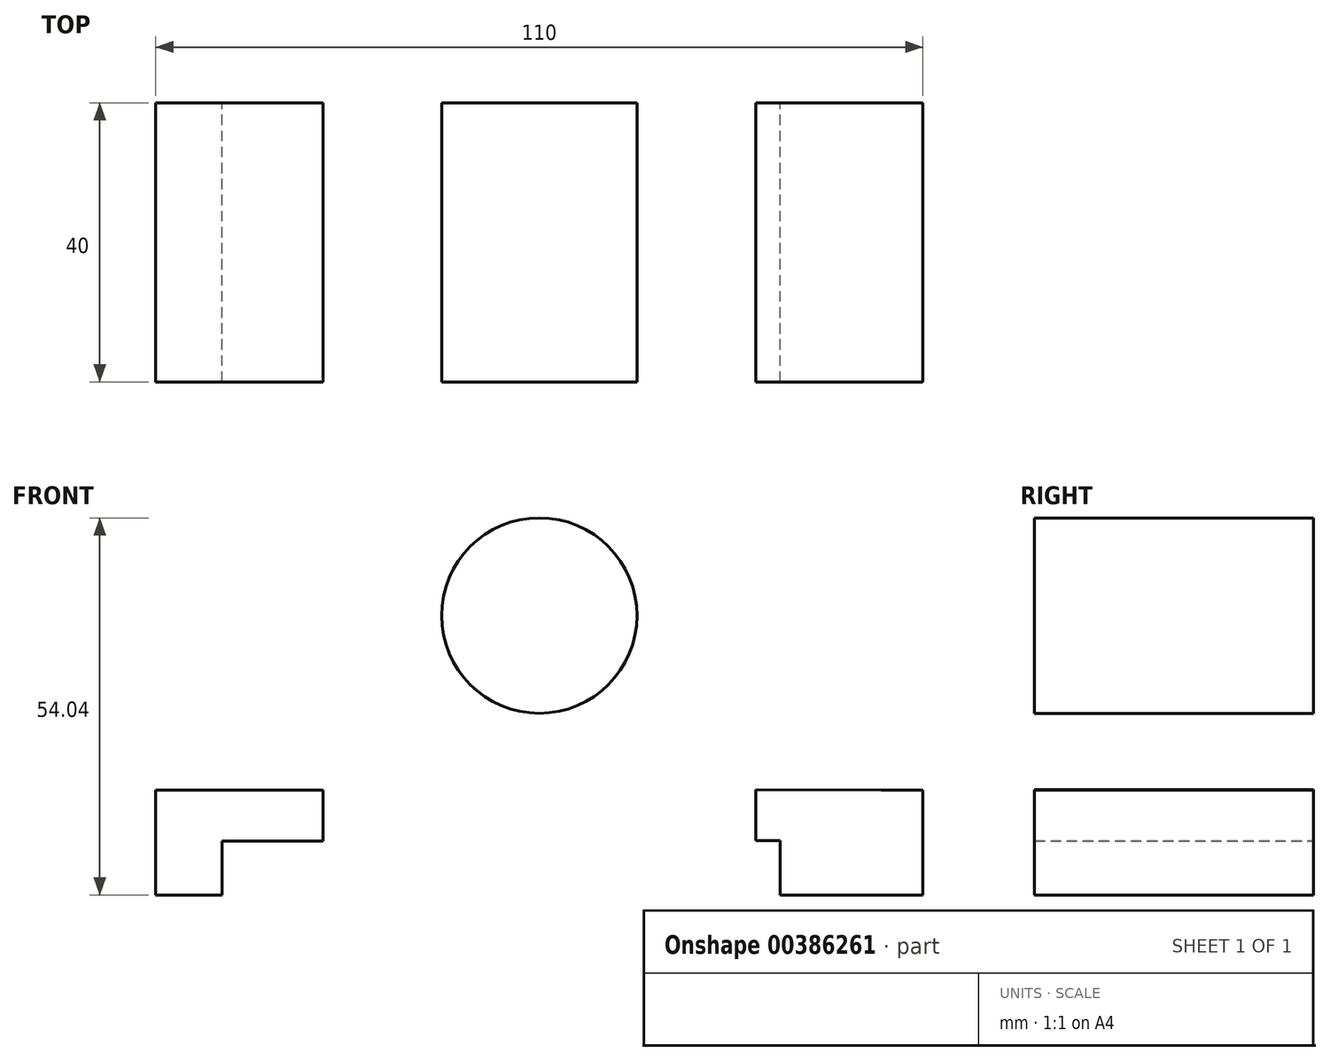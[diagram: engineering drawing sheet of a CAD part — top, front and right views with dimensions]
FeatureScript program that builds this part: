
annotation { "Feature Type Name" : "Feature", "Feature Type Description" : "" }
export const myFeature = defineFeature(function(context is Context, id is Id, definition is map)
    precondition{}
    {
        {
            var Q0;
            Q0=qCreatedBy(makeId("Front.planeOp"),FACE);
            var sketch = newSketch(context, id + "F0", { "sketchPlane" : qUnion([Q0])});
            skLineSegment(sketch, "E0", {"start": v(-42.27, 0) * mm, "end": v(67.73, 0) * mm});
            skLineSegment(sketch, "E1", {"start": v(67.73, 0) * mm, "end": v(67.73, 15) * mm});
            skLineSegment(sketch, "E2", {"start": v(37.73, 15.08) * mm, "end": v(37.73, 40.08) * mm});
            skLineSegment(sketch, "E3", {"start": v(-42.27, 0) * mm, "end": v(-42.27, 15) * mm});
            skLineSegment(sketch, "E4", {"start": v(-12.27, 15) * mm, "end": v(-12.27, 40) * mm});
            skLineSegment(sketch, "E5", {"start": v(-12.27, 40) * mm, "end": v(37.73, 40.08) * mm, "construction": true});
            skPoint(sketch, "E6", {"position": v(12.73, 40.04) * mm});
            skCircle(sketch, "E7", {"center": v(12.73, 40.04) * mm, "radius": 14 * mm});
            skPoint(sketch, "E8.endSnap0", {"position": v(-42.27, 7.5) * mm});
            skArc(sketch, "E9", {"start": v(37.73, 40) * mm, "mid": v(12.73, 65.04) * mm, "end": v(-12.27, 40) * mm});
            skLineSegment(sketch, "E10", {"start": v(-42.27, 15) * mm, "end": v(-12.27, 15) * mm});
            skLineSegment(sketch, "E11", {"start": v(-12.27, 15) * mm, "end": v(-18.27, 15) * mm});
            skLineSegment(sketch, "E12", {"start": v(-42.27, 15) * mm, "end": v(-36.27, 15) * mm});
            skLineSegment(sketch, "E13", {"start": v(-42.27, 0) * mm, "end": v(-32.77, 0) * mm});
            skLineSegment(sketch, "E14", {"start": v(-32.77, 0) * mm, "end": v(-21.77, 0) * mm});
            skLineSegment(sketch, "E15", {"start": v(-36.27, 15) * mm, "end": v(-36.27, 7.7) * mm});
            skLineSegment(sketch, "E16", {"start": v(-18.27, 15) * mm, "end": v(-18.27, 7.7) * mm});
            skLineSegment(sketch, "E17", {"start": v(-36.27, 7.7) * mm, "end": v(-18.27, 7.7) * mm});
            skLineSegment(sketch, "E18", {"start": v(-32.77, 0) * mm, "end": v(-32.77, 7.7) * mm});
            skLineSegment(sketch, "E19", {"start": v(-21.77, 0) * mm, "end": v(-21.77, 7.7) * mm});
            skLineSegment(sketch, "E20", {"start": v(67.73, 15) * mm, "end": v(61.73, 15) * mm});
            skLineSegment(sketch, "E21", {"start": v(37.73, 15.08) * mm, "end": v(43.73, 15.08) * mm});
            skLineSegment(sketch, "E22", {"start": v(61.73, 15) * mm, "end": v(43.73, 15.08) * mm});
            skLineSegment(sketch, "E23", {"start": v(67.73, 0) * mm, "end": v(58.23, 0) * mm});
            skLineSegment(sketch, "E24", {"start": v(58.23, 0) * mm, "end": v(47.23, 0) * mm});
            skLineSegment(sketch, "E25", {"start": v(61.73, 15) * mm, "end": v(61.73, 7.7) * mm});
            skLineSegment(sketch, "E26", {"start": v(43.73, 15.08) * mm, "end": v(43.73, 7.78) * mm});
            skLineSegment(sketch, "E27", {"start": v(61.73, 7.7) * mm, "end": v(43.73, 7.78) * mm});
            skLineSegment(sketch, "E28", {"start": v(58.23, 0) * mm, "end": v(58.23, 7.7) * mm});
            skLineSegment(sketch, "E29", {"start": v(47.23, 0) * mm, "end": v(47.23, 7.76) * mm});
            skSolve(sketch);
        }
        {
            var Q0;
            Q0=makeQuery(id+"F0.imprint","IMPRINT",FACE,{"disambiguationData":[TD([[makeQuery(id+"F0.imprint","IMPRINT",EDGE,{"derivedFrom":sQuery(id+"F0.wireOp",EDGE,"E1")}),1.0]])]});
            var Q1;
            Q1=makeQuery(id+"F0.imprint","IMPRINT",FACE,{"disambiguationData":[TD([[makeQuery(id+"F0.imprint","IMPRINT",EDGE,{"derivedFrom":sQuery(id+"F0.wireOp",EDGE,"E3")}),-1.0]])]});
            var Q2;
            Q2=makeQuery(id+"F0.imprint","IMPRINT",FACE,{"disambiguationData":[TD([[makeQuery(id+"F0.imprint","IMPRINT",EDGE,{"derivedFrom":sQuery(id+"F0.wireOp",EDGE,"E22")}),1.0]])]});
            var Q3;
            Q3=makeQuery(id+"F0.imprint","IMPRINT",FACE,{"disambiguationData":[TD([[makeQuery(id+"F0.imprint","IMPRINT",EDGE,{"derivedFrom":sQuery(id+"F0.wireOp",EDGE,"E10")}),-1.0]])]});
            var Q4;
            Q4=makeQuery(id+"F0.imprint","IMPRINT",FACE,{"disambiguationData":[TD([[makeQuery(id+"F0.imprint","IMPRINT",EDGE,{"derivedFrom":sQuery(id+"F0.wireOp",EDGE,"E0")}),1.0]])]});
            var Q5;
            Q5=makeQuery(id+"F0.imprint","IMPRINT",FACE,{"disambiguationData":[TD([[makeQuery(id+"F0.imprint","IMPRINT",EDGE,{"derivedFrom":sQuery(id+"F0.wireOp",EDGE,"E7")}),1.0]])]});
            var Q6;
            Q6=makeQuery(id+"F0.imprint","IMPRINT",FACE,{"disambiguationData":[TD([[makeQuery(id+"F0.imprint","IMPRINT",EDGE,{"derivedFrom":sQuery(id+"F0.wireOp",EDGE,"E14")}),1.0]])]});
            extrude(context, id + "F1", {"entities" : qUnion([Q0, Q1, Q2, Q3, Q4, Q5, Q6]), "depth" : 40 * mm});
        }
    });
